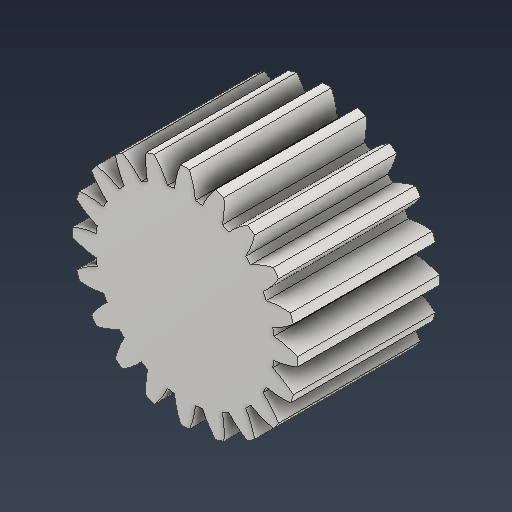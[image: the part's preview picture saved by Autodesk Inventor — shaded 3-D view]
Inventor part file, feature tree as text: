
AUTODESK INVENTOR PART (.ipt)
format: ipt  version: 2021 (Build 250183000, 183)  size: 269,824 bytes
history: native  units: mm (DEFAULTED — no unit token found)
features: plane x3, other x3, sketch x2, extrude x1
ambient origin geometry x8: Origin, YZ Plane, XZ Plane, XY Plane, X Axis, Y Axis, Z Axis, Center Point
bodies: Solid1 (feature_tree)
feature tree (9):
  extrude  "Extrusion1"  Depth=1.25mm TaperAngle=0.0deg
  plane  "Work Plane2"
  plane  "Work Plane8"
  plane  "Work Plane9"
  other  "Engrenagem reta"
  sketch  "Sketch1"  dims[d0=1.979988mm d1=1.25mm d2=0.0mm]
  sketch  "Sketch2"  dims[d3=1.8mm d4=10.0mm d5=0.0mm d16=3.597588mm d17=0.0mm d34=1.570796mm d39=0.0mm d41=0.0mm d43=3.597588mm d46=3.597588mm d47=0.0mm d48=0.0mm]
  other  "Srf1"
  other  "Diâmetro do flanco"
